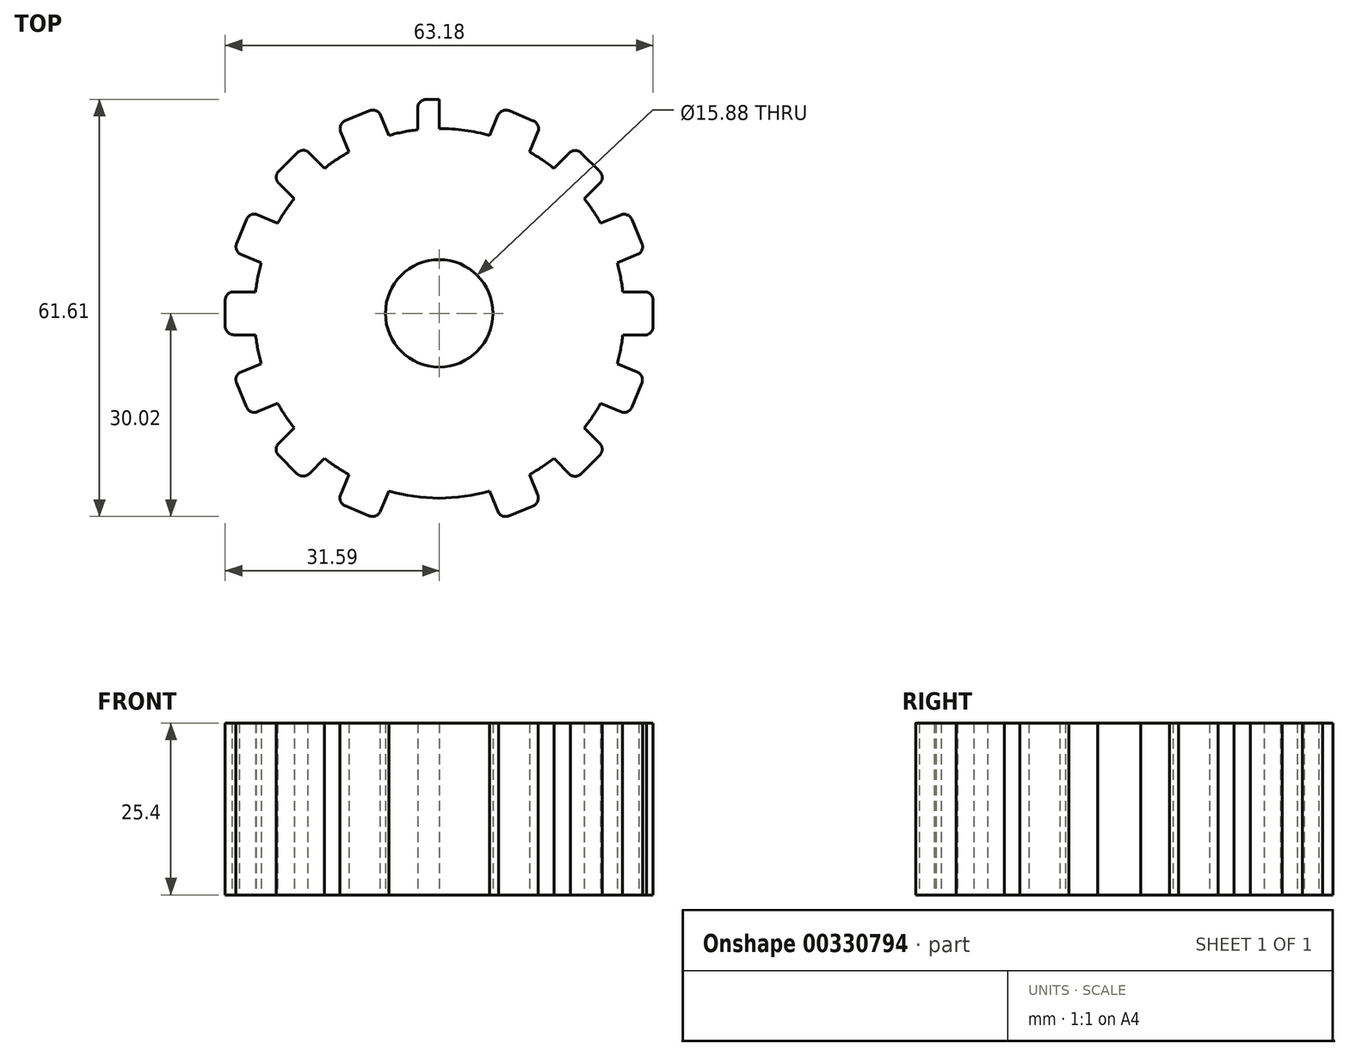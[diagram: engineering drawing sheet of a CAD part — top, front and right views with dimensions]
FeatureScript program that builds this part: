
annotation { "Feature Type Name" : "Feature", "Feature Type Description" : "" }
export const myFeature = defineFeature(function(context is Context, id is Id, definition is map)
    precondition{}
    {
        {
            var Q0;
            Q0=qCreatedBy(makeId("Top.planeOp"),FACE);
            var sketch = newSketch(context, id + "F0", { "sketchPlane" : qUnion([Q0])});
            skCircle(sketch, "E0", {"center": v(0, 0) * mm, "radius": 31.75 * mm});
            skCircle(sketch, "E1", {"center": v(0, 0) * mm, "radius": 7.94 * mm});
            skLineSegment(sketch, "E2", {"start": v(0, 0) * mm, "end": v(0, 42.4) * mm});
            skCircle(sketch, "E3", {"center": v(0, 0) * mm, "radius": 27.3 * mm});
            skLineSegment(sketch, "E4", {"start": v(-3.17, 27.12) * mm, "end": v(-3.17, 30.32) * mm});
            skLineSegment(sketch, "E5", {"start": v(-1.9, 31.6) * mm, "end": v(1.94, 31.6) * mm});
            skPoint(sketch, "E6.visualSharp", {"position": v(-3.18, 31.6) * mm});
            skArc(sketch, "E6.filletArc", {"start": v(-1.9, 31.6) * mm, "mid": v(-2.8, 31.22) * mm, "end": v(-3.18, 30.32) * mm});
            skPoint(sketch, "E7.visualSharp", {"position": v(3.17, 31.6) * mm});
            skArc(sketch, "E7.filletArc", {"start": v(3.18, 30.61) * mm, "mid": v(2.73, 31.32) * mm, "end": v(1.94, 31.6) * mm});
            skLineSegment(sketch, "E8", {"start": v(3.18, 30.61) * mm, "end": v(3.18, 27.12) * mm});
            skArc(sketch, "E9.1.4", {"start": v(3.17, 30.61) * mm, "mid": v(2.73, 31.32) * mm, "end": v(1.94, 31.6) * mm});
            skLineSegment(sketch, "E9.2.2", {"start": v(-3.17, 27.12) * mm, "end": v(-3.18, 30.32) * mm});
            skArc(sketch, "E9.2.4", {"start": v(3.17, 30.61) * mm, "mid": v(2.73, 31.32) * mm, "end": v(1.94, 31.6) * mm});
            skLineSegment(sketch, "E9.anchor1", {"start": v(0, 0) * mm, "end": v(-1.9, 31.6) * mm, "construction": true});
            skLineSegment(sketch, "E9.anchor2", {"start": v(0, 0) * mm, "end": v(-1.9, 31.6) * mm, "construction": true});
            skLineSegment(sketch, "E10.1.0", {"start": v(7.44, 26.27) * mm, "end": v(8.67, 29.23) * mm});
            skArc(sketch, "E10.1.1", {"start": v(10.33, 29.92) * mm, "mid": v(9.36, 29.92) * mm, "end": v(8.67, 29.23) * mm});
            skLineSegment(sketch, "E10.1.2", {"start": v(10.33, 29.92) * mm, "end": v(13.88, 28.44) * mm});
            skArc(sketch, "E10.1.3", {"start": v(14.65, 27.07) * mm, "mid": v(14.5, 27.89) * mm, "end": v(13.88, 28.44) * mm});
            skLineSegment(sketch, "E10.1.4", {"start": v(14.65, 27.07) * mm, "end": v(13.31, 23.84) * mm});
            skLineSegment(sketch, "E10.2.0", {"start": v(16.93, 21.42) * mm, "end": v(19.2, 23.69) * mm});
            skArc(sketch, "E10.2.1", {"start": v(21, 23.69) * mm, "mid": v(20.1, 24.06) * mm, "end": v(19.2, 23.69) * mm});
            skLineSegment(sketch, "E10.2.2", {"start": v(21, 23.69) * mm, "end": v(23.7, 20.97) * mm});
            skArc(sketch, "E10.2.3", {"start": v(23.9, 19.4) * mm, "mid": v(24.07, 20.22) * mm, "end": v(23.7, 20.97) * mm});
            skLineSegment(sketch, "E10.2.4", {"start": v(23.9, 19.4) * mm, "end": v(21.42, 16.93) * mm});
            skLineSegment(sketch, "E10.anchor2", {"start": v(0, 0) * mm, "end": v(16.93, 21.42) * mm, "construction": true});
            skLineSegment(sketch, "E11.1.0", {"start": v(23.84, 13.31) * mm, "end": v(26.8, 14.54) * mm});
            skLineSegment(sketch, "E11.1.1", {"start": v(28.46, 13.85) * mm, "end": v(29.93, 10.3) * mm});
            skLineSegment(sketch, "E11.1.2", {"start": v(29.5, 8.78) * mm, "end": v(26.27, 7.44) * mm});
            skArc(sketch, "E11.1.3", {"start": v(29.5, 8.78) * mm, "mid": v(29.98, 9.46) * mm, "end": v(29.93, 10.3) * mm});
            skArc(sketch, "E11.1.4", {"start": v(28.46, 13.85) * mm, "mid": v(27.77, 14.54) * mm, "end": v(26.8, 14.54) * mm});
            skLineSegment(sketch, "E11.2.0", {"start": v(27.12, 3.18) * mm, "end": v(30.32, 3.18) * mm});
            skLineSegment(sketch, "E11.2.1", {"start": v(31.6, 1.9) * mm, "end": v(31.6, -1.94) * mm});
            skLineSegment(sketch, "E11.2.2", {"start": v(30.61, -3.17) * mm, "end": v(27.12, -3.17) * mm});
            skArc(sketch, "E11.2.3", {"start": v(30.61, -3.17) * mm, "mid": v(31.32, -2.73) * mm, "end": v(31.6, -1.94) * mm});
            skArc(sketch, "E11.2.4", {"start": v(31.6, 1.9) * mm, "mid": v(31.22, 2.8) * mm, "end": v(30.32, 3.18) * mm});
            skLineSegment(sketch, "E11.anchor2", {"start": v(0, 0) * mm, "end": v(27.12, 3.18) * mm, "construction": true});
            skLineSegment(sketch, "E12.1.0", {"start": v(27.07, -14.65) * mm, "end": v(23.84, -13.31) * mm});
            skLineSegment(sketch, "E12.1.1", {"start": v(26.27, -7.44) * mm, "end": v(29.23, -8.67) * mm});
            skArc(sketch, "E12.1.2", {"start": v(29.92, -10.33) * mm, "mid": v(29.92, -9.36) * mm, "end": v(29.23, -8.67) * mm});
            skLineSegment(sketch, "E12.1.3", {"start": v(29.92, -10.33) * mm, "end": v(28.44, -13.88) * mm});
            skArc(sketch, "E12.1.4", {"start": v(27.07, -14.65) * mm, "mid": v(27.89, -14.5) * mm, "end": v(28.44, -13.88) * mm});
            skLineSegment(sketch, "E12.2.0", {"start": v(19.4, -23.9) * mm, "end": v(16.93, -21.42) * mm});
            skLineSegment(sketch, "E12.2.1", {"start": v(21.42, -16.93) * mm, "end": v(23.69, -19.2) * mm});
            skArc(sketch, "E12.2.2", {"start": v(23.69, -21) * mm, "mid": v(24.06, -20.1) * mm, "end": v(23.69, -19.2) * mm});
            skLineSegment(sketch, "E12.2.3", {"start": v(23.69, -21) * mm, "end": v(20.97, -23.7) * mm});
            skArc(sketch, "E12.2.4", {"start": v(19.4, -23.9) * mm, "mid": v(20.22, -24.07) * mm, "end": v(20.97, -23.7) * mm});
            skLineSegment(sketch, "E12.anchor1", {"start": v(0, 0) * mm, "end": v(27.12, -3.17) * mm, "construction": true});
            skLineSegment(sketch, "E12.anchor2", {"start": v(0, 0) * mm, "end": v(16.93, -21.42) * mm, "construction": true});
            skLineSegment(sketch, "E13.1.0", {"start": v(3.18, -27.12) * mm, "end": v(3.18, -30.32) * mm});
            skLineSegment(sketch, "E13.1.1", {"start": v(-3.17, -30.61) * mm, "end": v(-3.17, -27.12) * mm});
            skArc(sketch, "E13.1.2", {"start": v(-3.17, -30.61) * mm, "mid": v(-2.73, -31.32) * mm, "end": v(-1.94, -31.6) * mm});
            skLineSegment(sketch, "E13.1.3", {"start": v(1.9, -31.6) * mm, "end": v(-1.94, -31.6) * mm});
            skArc(sketch, "E13.1.4", {"start": v(1.9, -31.6) * mm, "mid": v(2.8, -31.22) * mm, "end": v(3.18, -30.32) * mm});
            skLineSegment(sketch, "E13.1.5", {"start": v(8.78, -29.5) * mm, "end": v(7.44, -26.27) * mm});
            skArc(sketch, "E13.1.6", {"start": v(8.78, -29.5) * mm, "mid": v(9.46, -29.98) * mm, "end": v(10.3, -29.93) * mm});
            skLineSegment(sketch, "E13.1.7", {"start": v(13.85, -28.46) * mm, "end": v(10.3, -29.93) * mm});
            skArc(sketch, "E13.1.8", {"start": v(13.85, -28.46) * mm, "mid": v(14.54, -27.77) * mm, "end": v(14.54, -26.8) * mm});
            skLineSegment(sketch, "E13.1.9", {"start": v(13.31, -23.84) * mm, "end": v(14.54, -26.8) * mm});
            skLineSegment(sketch, "E13.2.0", {"start": v(-16.93, -21.42) * mm, "end": v(-19.2, -23.69) * mm});
            skLineSegment(sketch, "E13.2.1", {"start": v(-23.9, -19.4) * mm, "end": v(-21.42, -16.93) * mm});
            skArc(sketch, "E13.2.2", {"start": v(-23.9, -19.4) * mm, "mid": v(-24.07, -20.22) * mm, "end": v(-23.7, -20.97) * mm});
            skLineSegment(sketch, "E13.2.3", {"start": v(-21, -23.69) * mm, "end": v(-23.7, -20.97) * mm});
            skArc(sketch, "E13.2.4", {"start": v(-21, -23.69) * mm, "mid": v(-20.1, -24.06) * mm, "end": v(-19.2, -23.69) * mm});
            skLineSegment(sketch, "E13.2.5", {"start": v(-14.65, -27.07) * mm, "end": v(-13.31, -23.84) * mm});
            skArc(sketch, "E13.2.6", {"start": v(-14.65, -27.07) * mm, "mid": v(-14.5, -27.89) * mm, "end": v(-13.88, -28.44) * mm});
            skLineSegment(sketch, "E13.2.7", {"start": v(-10.33, -29.92) * mm, "end": v(-13.88, -28.44) * mm});
            skArc(sketch, "E13.2.8", {"start": v(-10.33, -29.92) * mm, "mid": v(-9.36, -29.92) * mm, "end": v(-8.67, -29.23) * mm});
            skLineSegment(sketch, "E13.2.9", {"start": v(-7.44, -26.27) * mm, "end": v(-8.67, -29.23) * mm});
            skLineSegment(sketch, "E13.2.10", {"start": v(-3.17, -30.61) * mm, "end": v(-3.17, -27.12) * mm});
            skArc(sketch, "E13.2.11", {"start": v(-3.17, -30.61) * mm, "mid": v(-2.73, -31.32) * mm, "end": v(-1.94, -31.6) * mm});
            skLineSegment(sketch, "E13.2.12", {"start": v(1.9, -31.6) * mm, "end": v(-1.94, -31.6) * mm});
            skArc(sketch, "E13.2.13", {"start": v(1.9, -31.6) * mm, "mid": v(2.8, -31.22) * mm, "end": v(3.18, -30.32) * mm});
            skLineSegment(sketch, "E13.2.14", {"start": v(3.18, -27.12) * mm, "end": v(3.18, -30.32) * mm});
            skLineSegment(sketch, "E13.anchor1", {"start": v(0, 0) * mm, "end": v(23.69, -19.2) * mm, "construction": true});
            skLineSegment(sketch, "E13.anchor2", {"start": v(0, 0) * mm, "end": v(-19.2, -23.69) * mm, "construction": true});
            skLineSegment(sketch, "E14.1.0", {"start": v(-27.07, 14.65) * mm, "end": v(-23.84, 13.31) * mm});
            skLineSegment(sketch, "E14.1.1", {"start": v(-26.27, 7.44) * mm, "end": v(-29.23, 8.67) * mm});
            skArc(sketch, "E14.1.2", {"start": v(-29.92, 10.33) * mm, "mid": v(-29.92, 9.36) * mm, "end": v(-29.23, 8.67) * mm});
            skArc(sketch, "E14.1.3", {"start": v(-27.07, 14.65) * mm, "mid": v(-27.89, 14.5) * mm, "end": v(-28.44, 13.88) * mm});
            skLineSegment(sketch, "E14.1.4", {"start": v(-29.92, 10.33) * mm, "end": v(-28.44, 13.88) * mm});
            skLineSegment(sketch, "E14.1.5", {"start": v(-30.61, 3.17) * mm, "end": v(-27.12, 3.17) * mm});
            skArc(sketch, "E14.1.6", {"start": v(-30.61, 3.17) * mm, "mid": v(-31.32, 2.73) * mm, "end": v(-31.6, 1.94) * mm});
            skLineSegment(sketch, "E14.1.7", {"start": v(-31.6, -1.9) * mm, "end": v(-31.6, 1.94) * mm});
            skArc(sketch, "E14.1.8", {"start": v(-31.6, -1.9) * mm, "mid": v(-31.22, -2.8) * mm, "end": v(-30.32, -3.18) * mm});
            skLineSegment(sketch, "E14.1.9", {"start": v(-27.12, -3.18) * mm, "end": v(-30.32, -3.18) * mm});
            skLineSegment(sketch, "E14.1.10", {"start": v(-29.5, -8.78) * mm, "end": v(-26.27, -7.44) * mm});
            skArc(sketch, "E14.1.11", {"start": v(-29.5, -8.78) * mm, "mid": v(-29.98, -9.46) * mm, "end": v(-29.93, -10.3) * mm});
            skLineSegment(sketch, "E14.1.12", {"start": v(-28.46, -13.85) * mm, "end": v(-29.93, -10.3) * mm});
            skArc(sketch, "E14.1.13", {"start": v(-28.46, -13.85) * mm, "mid": v(-27.77, -14.54) * mm, "end": v(-26.8, -14.54) * mm});
            skLineSegment(sketch, "E14.1.14", {"start": v(-23.84, -13.31) * mm, "end": v(-26.8, -14.54) * mm});
            skLineSegment(sketch, "E14.2.0", {"start": v(3.17, 30.61) * mm, "end": v(3.17, 27.12) * mm});
            skLineSegment(sketch, "E14.2.1", {"start": v(-3.18, 27.12) * mm, "end": v(-3.18, 30.32) * mm});
            skLineSegment(sketch, "E14.2.5", {"start": v(-8.78, 29.5) * mm, "end": v(-7.44, 26.27) * mm});
            skArc(sketch, "E14.2.6", {"start": v(-8.78, 29.5) * mm, "mid": v(-9.46, 29.98) * mm, "end": v(-10.3, 29.93) * mm});
            skLineSegment(sketch, "E14.2.7", {"start": v(-13.85, 28.46) * mm, "end": v(-10.3, 29.93) * mm});
            skArc(sketch, "E14.2.8", {"start": v(-13.85, 28.46) * mm, "mid": v(-14.54, 27.77) * mm, "end": v(-14.54, 26.8) * mm});
            skLineSegment(sketch, "E14.2.9", {"start": v(-13.31, 23.84) * mm, "end": v(-14.54, 26.8) * mm});
            skLineSegment(sketch, "E14.2.10", {"start": v(-19.4, 23.9) * mm, "end": v(-16.93, 21.42) * mm});
            skArc(sketch, "E14.2.11", {"start": v(-19.4, 23.9) * mm, "mid": v(-20.22, 24.07) * mm, "end": v(-20.97, 23.7) * mm});
            skLineSegment(sketch, "E14.2.12", {"start": v(-23.69, 21) * mm, "end": v(-20.97, 23.7) * mm});
            skArc(sketch, "E14.2.13", {"start": v(-23.69, 21) * mm, "mid": v(-24.06, 20.1) * mm, "end": v(-23.69, 19.2) * mm});
            skLineSegment(sketch, "E14.2.14", {"start": v(-21.42, 16.93) * mm, "end": v(-23.69, 19.2) * mm});
            skLineSegment(sketch, "E14.anchor1", {"start": v(0, 0) * mm, "end": v(-23.9, -19.4) * mm, "construction": true});
            skLineSegment(sketch, "E14.anchor2", {"start": v(0, 0) * mm, "end": v(3.17, 30.61) * mm, "construction": true});
            skSolve(sketch);
        }
        {
            var Q0;
            Q0=makeQuery(id+"F0.imprint","IMPRINT",FACE,{"disambiguationData":[TD([[makeQuery(id+"F0.imprint","IMPRINT",EDGE,{"derivedFrom":sQuery(id+"F0.wireOp",EDGE,"E1")}),-1.0]])]});
            var Q1;
            {var subQ0=sQuery(id+"F0.wireOp",EDGE,"E14.2.5");Q1=makeQuery(id+"F0.imprint","IMPRINT",FACE,{"disambiguationData":[TD([[makeQuery(id+"F0.imprint","IMPRINT",EDGE,{"derivedFrom":subQ0}),-1.0]])]});}
            var Q2;
            {var subQ0=sQuery(id+"F0.wireOp",EDGE,"E14.2.10");Q2=makeQuery(id+"F0.imprint","IMPRINT",FACE,{"disambiguationData":[TD([[makeQuery(id+"F0.imprint","IMPRINT",EDGE,{"derivedFrom":subQ0}),-1.0]])]});}
            var Q3;
            {var subQ0=sQuery(id+"F0.wireOp",EDGE,"E14.1.0");Q3=makeQuery(id+"F0.imprint","IMPRINT",FACE,{"disambiguationData":[TD([[makeQuery(id+"F0.imprint","IMPRINT",EDGE,{"derivedFrom":subQ0}),-1.0]])]});}
            var Q4;
            {var subQ0=sQuery(id+"F0.wireOp",EDGE,"E14.1.5");Q4=makeQuery(id+"F0.imprint","IMPRINT",FACE,{"disambiguationData":[TD([[makeQuery(id+"F0.imprint","IMPRINT",EDGE,{"derivedFrom":subQ0}),-1.0]])]});}
            var Q5;
            {var subQ0=sQuery(id+"F0.wireOp",EDGE,"E14.1.10");Q5=makeQuery(id+"F0.imprint","IMPRINT",FACE,{"disambiguationData":[TD([[makeQuery(id+"F0.imprint","IMPRINT",EDGE,{"derivedFrom":subQ0}),-1.0]])]});}
            var Q6;
            {var subQ1=sQuery(id+"F0.wireOp",EDGE,"E13.2.0");Q6=makeQuery(id+"F0.imprint","IMPRINT",FACE,{"disambiguationData":[TD([[makeQuery(id+"F0.imprint","IMPRINT",EDGE,{"derivedFrom":subQ1}),-1.0]])]});}
            var Q7;
            {var subQ0=sQuery(id+"F0.wireOp",EDGE,"E13.2.5");Q7=makeQuery(id+"F0.imprint","IMPRINT",FACE,{"disambiguationData":[TD([[makeQuery(id+"F0.imprint","IMPRINT",EDGE,{"derivedFrom":subQ0}),-1.0]])]});}
            var Q8;
            {var subQ0=sQuery(id+"F0.wireOp",EDGE,"E13.2.10");Q8=makeQuery(id+"F0.imprint","IMPRINT",FACE,{"disambiguationData":[TD([[makeQuery(id+"F0.imprint","IMPRINT",EDGE,{"derivedFrom":subQ0}),-1.0]])]});}
            var Q9;
            {var subQ0=sQuery(id+"F0.wireOp",EDGE,"E13.1.5");Q9=makeQuery(id+"F0.imprint","IMPRINT",FACE,{"disambiguationData":[TD([[makeQuery(id+"F0.imprint","IMPRINT",EDGE,{"derivedFrom":subQ0}),-1.0]])]});}
            var Q10;
            {var subQ0=sQuery(id+"F0.wireOp",EDGE,"E12.2.0");Q10=makeQuery(id+"F0.imprint","IMPRINT",FACE,{"disambiguationData":[TD([[makeQuery(id+"F0.imprint","IMPRINT",EDGE,{"derivedFrom":subQ0}),-1.0]])]});}
            var Q11;
            {var subQ1=sQuery(id+"F0.wireOp",EDGE,"E12.1.0");Q11=makeQuery(id+"F0.imprint","IMPRINT",FACE,{"disambiguationData":[TD([[makeQuery(id+"F0.imprint","IMPRINT",EDGE,{"derivedFrom":subQ1}),-1.0]])]});}
            var Q12;
            {var subQ1=sQuery(id+"F0.wireOp",EDGE,"E11.2.0");Q12=makeQuery(id+"F0.imprint","IMPRINT",FACE,{"disambiguationData":[TD([[makeQuery(id+"F0.imprint","IMPRINT",EDGE,{"derivedFrom":subQ1}),-1.0]])]});}
            var Q13;
            {var subQ1=sQuery(id+"F0.wireOp",EDGE,"E11.1.0");Q13=makeQuery(id+"F0.imprint","IMPRINT",FACE,{"disambiguationData":[TD([[makeQuery(id+"F0.imprint","IMPRINT",EDGE,{"derivedFrom":subQ1}),-1.0]])]});}
            var Q14;
            {var subQ0=sQuery(id+"F0.wireOp",EDGE,"E10.2.0");Q14=makeQuery(id+"F0.imprint","IMPRINT",FACE,{"disambiguationData":[TD([[makeQuery(id+"F0.imprint","IMPRINT",EDGE,{"derivedFrom":subQ0}),-1.0]])]});}
            var Q15;
            {var subQ0=sQuery(id+"F0.wireOp",EDGE,"E10.1.0");Q15=makeQuery(id+"F0.imprint","IMPRINT",FACE,{"disambiguationData":[TD([[makeQuery(id+"F0.imprint","IMPRINT",EDGE,{"derivedFrom":subQ0}),-1.0]])]});}
            var Q16;
            {var subQ1=sQuery(id+"F0.wireOp",EDGE,"E14.2.0");Q16=makeQuery(id+"F0.imprint","IMPRINT",FACE,{"disambiguationData":[TD([[makeQuery(id+"F0.imprint","IMPRINT",EDGE,{"derivedFrom":subQ1}),-1.0]])]});}
            var Q17;
            {var subQ1=sQuery(id+"F0.wireOp",EDGE,"E14.2.1");Q17=makeQuery(id+"F0.imprint","IMPRINT",FACE,{"disambiguationData":[TD([[makeQuery(id+"F0.imprint","IMPRINT",EDGE,{"derivedFrom":subQ1}),-1.0]])]});}
            extrude(context, id + "F1", {"entities" : qUnion([Q0, Q1, Q2, Q3, Q4, Q5, Q6, Q7, Q8, Q9, Q10, Q11, Q12, Q13, Q14, Q15, Q16, Q17]), "depth" : 25.4 * mm});
        }
    });
